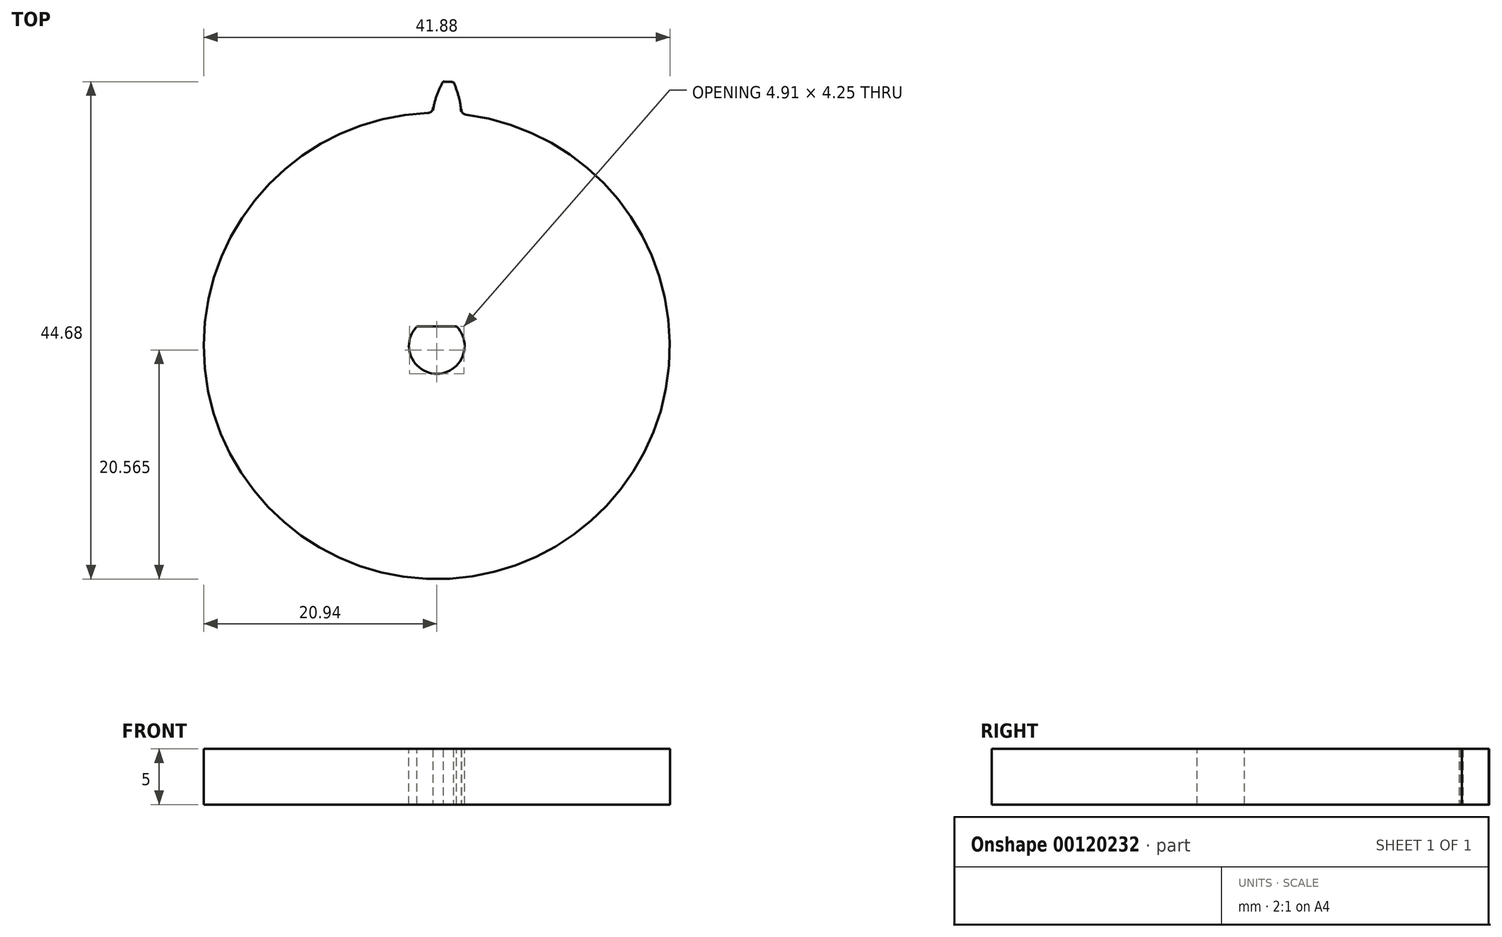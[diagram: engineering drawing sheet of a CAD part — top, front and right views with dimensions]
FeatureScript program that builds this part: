
annotation { "Feature Type Name" : "Feature", "Feature Type Description" : "" }
export const myFeature = defineFeature(function(context is Context, id is Id, definition is map)
    precondition{}
    {
        {
            var Q0;
            Q0=qCreatedBy(makeId("Front.planeOp"),FACE);
            var sketch = newSketch(context, id + "F0", { "sketchPlane" : qUnion([Q0])});
            skLineSegment(sketch, "E0", {"start": v(0, 72.27) * mm, "end": v(0, -50.25) * mm, "construction": true});
            skSolve(sketch);
        }
        {
            var Q0;
            Q0=qCreatedBy(makeId("Top.planeOp"),FACE);
            var sketch = newSketch(context, id + "F1", { "sketchPlane" : qUnion([Q0])});
            skCircle(sketch, "E1", {"center": v(0, 0) * mm, "radius": 22.5 * mm, "construction": true});
            skCircle(sketch, "E2", {"center": v(0, 0) * mm, "radius": 20.94 * mm});
            skSolve(sketch);
        }
        {
            var Q0;
            Q0=qSketchRegion(id+"F1",true);
            extrude(context, id + "F2", {"entities" : qUnion([Q0]), "depth" : 5 * mm});
        }
        {
            var Q0;
            Q0=makeQuery(id+"F2.opExtrude","CAP_FACE",FACE,{"disambiguationData":[OSD([sQuery(id+"F1.wireOp",EDGE,"E2"),sQuery(id+"F1.wireOp",EDGE,"lKhcHiEn-qWT4-b5GR-9CCX-N4hY3lJjeW35"),sQuery(id+"F1.wireOp",EDGE,"zsuhm7zz-1LAn-hH0Z-Fbhr-HMJ1RvOiH2OX")])],"isStart":false});
            var sketch = newSketch(context, id + "F3", { "sketchPlane" : qUnion([Q0])});
            skArc(sketch, "E3", {"start": v(-1.79, 1.75) * mm, "mid": v(0, -2.5) * mm, "end": v(1.79, 1.75) * mm});
            skLineSegment(sketch, "E4", {"start": v(-1.79, 1.75) * mm, "end": v(1.79, 1.75) * mm});
            skPoint(sketch, "E5", {"position": v(0, 2.5) * mm});
            skArc(sketch, "E6", {"start": v(-1.79, 1.75) * mm, "mid": v(0, 2.5) * mm, "end": v(1.79, 1.75) * mm, "construction": true});
            skSolve(sketch);
        }
        {
            var Q0;
            Q0=qSketchRegion(id+"F3",true);
            extrude(context, id + "F4", {"entities" : qUnion([Q0]), "operationType" : NewBodyOperationType.REMOVE, "endBound" : BoundingType.THROUGH_ALL, "oppositeDirection" : true, "depth" : 25 * mm});
        }
        {
            var Q0;
            Q0=qCreatedBy(makeId("Top.planeOp"),FACE);
            var sketch = newSketch(context, id + "F5", { "sketchPlane" : qUnion([Q0])});
            skLineSegment(sketch, "E7", {"start": v(0, 0) * mm, "end": v(0, 29.7) * mm, "construction": true});
            skLineSegment(sketch, "E8", {"start": v(0, 0) * mm, "end": v(-10.47, 28.76) * mm, "construction": true});
            skLineSegment(sketch, "E9", {"start": v(0, 22.5) * mm, "end": v(-7.23, 19.87) * mm, "construction": true});
            skCircle(sketch, "E10", {"center": v(0, 0) * mm, "radius": 22.5 * mm, "construction": true});
            skCircle(sketch, "E11", {"center": v(0, 0) * mm, "radius": 23.75 * mm, "construction": true});
            skArc(sketch, "E12", {"start": v(-0.8, 20.92) * mm, "mid": v(-0.91, -20.92) * mm, "end": v(2.61, 20.77) * mm, "construction": true});
            skCircle(sketch, "E13", {"center": v(0, 0) * mm, "radius": 21.14 * mm, "construction": true});
            skCircle(sketch, "E14", {"center": v(8.83, 19.21) * mm, "radius": 9.42 * mm, "construction": true});
            skCircle(sketch, "E15", {"center": v(5.74, 20.35) * mm, "radius": 6.13 * mm, "construction": true});
            skArc(sketch, "E16", {"start": v(0.57, 23.74) * mm, "mid": v(0.26, 23.13) * mm, "end": v(0, 22.5) * mm});
            skArc(sketch, "E17", {"start": v(0, 22.5) * mm, "mid": v(-0.2, 21.83) * mm, "end": v(-0.34, 21.14) * mm});
            skLineSegment(sketch, "E18", {"start": v(-0.34, 21.4) * mm, "end": v(-0.34, 21.14) * mm});
            skLineSegment(sketch, "E19", {"start": v(-0.34, 20.93) * mm, "end": v(0, 0) * mm, "construction": true});
            skArc(sketch, "E20", {"start": v(1.96, 22.41) * mm, "mid": v(0.98, 22.48) * mm, "end": v(0, 22.5) * mm});
            skLineSegment(sketch, "E21", {"start": v(0, 0) * mm, "end": v(0.98, 22.48) * mm, "construction": true});
            skLineSegment(sketch, "E22", {"start": v(0.56, 12.86) * mm, "end": v(0.98, 22.48) * mm, "construction": true});
            skArc(sketch, "E23", {"start": v(1.04, 23.73) * mm, "mid": v(0.8, 23.74) * mm, "end": v(0.57, 23.74) * mm});
            skArc(sketch, "E24.MirrorCS", {"start": v(1.04, 23.73) * mm, "mid": v(1.27, 23.72) * mm, "end": v(1.5, 23.7) * mm});
            skArc(sketch, "E25.MirrorCS", {"start": v(1.5, 23.7) * mm, "mid": v(1.76, 23.07) * mm, "end": v(1.96, 22.41) * mm});
            skArc(sketch, "E26.MirrorCS", {"start": v(1.96, 22.41) * mm, "mid": v(2.11, 21.73) * mm, "end": v(2.18, 21.03) * mm});
            skLineSegment(sketch, "E27.MirrorCS", {"start": v(2.2, 21.29) * mm, "end": v(2.18, 21.03) * mm});
            skPoint(sketch, "E28.visualSharp", {"position": v(-0.34, 20.93) * mm});
            skArc(sketch, "E28.filletArc", {"start": v(-0.8, 20.92) * mm, "mid": v(-0.47, 21.07) * mm, "end": v(-0.34, 21.4) * mm});
            skArc(sketch, "E29.MirrorCS", {"start": v(2.61, 20.77) * mm, "mid": v(2.3, 20.95) * mm, "end": v(2.2, 21.29) * mm});
            skPoint(sketch, "E30.orphan", {"position": v(2.16, 20.83) * mm});
            skArc(sketch, "E31", {"start": v(-0.8, 20.92) * mm, "mid": v(0.91, 20.92) * mm, "end": v(2.61, 20.77) * mm});
            skSolve(sketch);
        }
        {
            var Q0;
            Q0=qSketchRegion(id+"F5",true);
            extrude(context, id + "F6", {"entities" : qUnion([Q0]), "operationType" : NewBodyOperationType.ADD, "depth" : 5 * mm});
        }
    });
